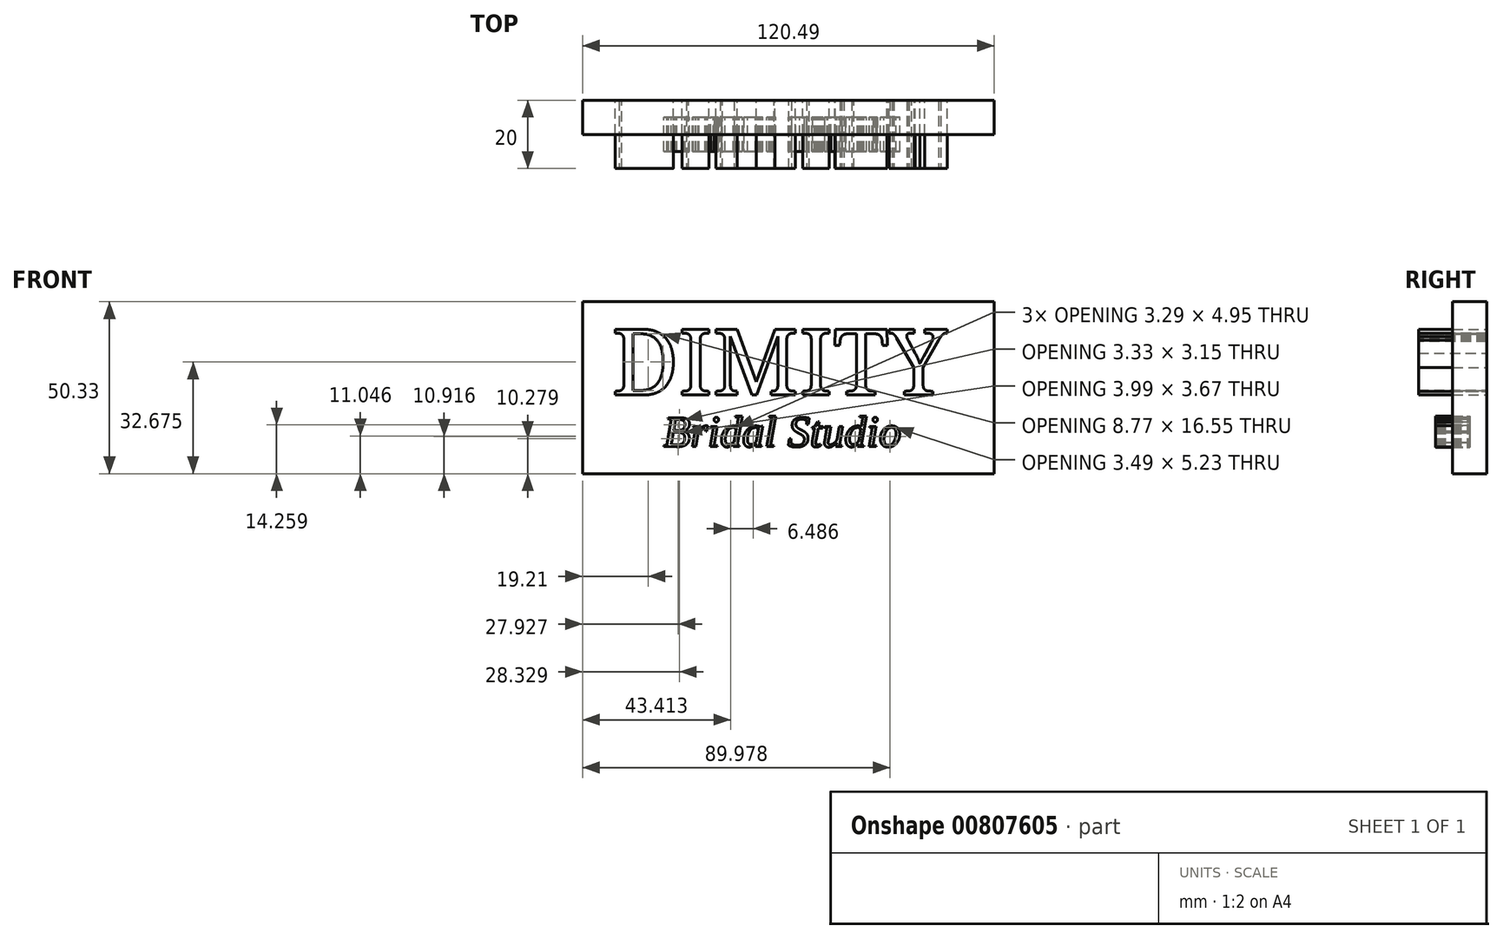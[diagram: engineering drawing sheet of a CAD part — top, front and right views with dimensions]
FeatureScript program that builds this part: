
annotation { "Feature Type Name" : "Feature", "Feature Type Description" : "" }
export const myFeature = defineFeature(function(context is Context, id is Id, definition is map)
    precondition{}
    {
        {
            var Q0;
            Q0=qCreatedBy(makeId("Front.planeOp"),FACE);
            var sketch = newSketch(context, id + "F0", { "sketchPlane" : qUnion([Q0])});
            skText(sketch, "E0", { "text": "DIMITY\n", "fontName": "NotoSerif-Regular.ttf"});
            const initialGuessF0  = {"E0": [-0.05114, -0.00939, 1, 0, 0.01943]};
            skSetInitialGuess(sketch, initialGuessF0);
            skSolve(sketch);
        }
        {
            var Q0;
            Q0=qCreatedBy(makeId("Front.planeOp"),FACE);
            var sketch = newSketch(context, id + "F1", { "sketchPlane" : qUnion([Q0])});
            skText(sketch, "E1", { "text": "Bridal Studio", "fontName": "Tinos-Italic.ttf"});
            const initialGuessF1  = {"E1": [-0.03598, -0.02451, 1, 0, 0.00934]};
            skSetInitialGuess(sketch, initialGuessF1);
            skSolve(sketch);
        }
        {
            var Q0;
            Q0 = qSketchRegion(id + "F0", true);
            extrude(context, id + "F2", {"entities" : qUnion([Q0]), "endBound" : BoundingType.SYMMETRIC, "depth" : 20 * mm, "offsetDistance" : 25 * mm});
        }
        {
            var Q0;
            Q0 = qSketchRegion(id + "F1", true);
            extrude(context, id + "F3", {"entities" : qUnion([Q0]), "endBound" : BoundingType.SYMMETRIC, "depth" : 10 * mm, "offsetDistance" : 25 * mm});
        }
        {
            var Q0;
            Q0=qCreatedBy(makeId("Front.planeOp"),FACE);
            var sketch = newSketch(context, id + "F4", { "sketchPlane" : qUnion([Q0])});
            skLineSegment(sketch, "E2.bottom", {"start": v(-59.65, 17.91) * mm, "end": v(60.84, 17.91) * mm});
            skLineSegment(sketch, "E2.top", {"start": v(-59.65, -32.42) * mm, "end": v(60.84, -32.42) * mm});
            skLineSegment(sketch, "E2.left", {"start": v(-59.65, 17.91) * mm, "end": v(-59.65, -32.42) * mm});
            skLineSegment(sketch, "E2.right", {"start": v(60.84, 17.91) * mm, "end": v(60.84, -32.42) * mm});
            skSolve(sketch);
        }
        {
            var Q0;
            Q0=makeQuery(id+"F4.imprint","IMPRINT",FACE,{"disambiguationData":[TD([[makeQuery(id+"F4.imprint","IMPRINT",EDGE,{"derivedFrom":sQuery(id+"F4.wireOp",EDGE,"E2.bottom")}),-1.0]])]});
            var Q1;
            Q1=makeQuery(id+"F2.opExtrude","CAP_FACE",FACE,{"disambiguationData":[OSD([sQuery(id+"F0.wireOp",EDGE,"E0.sketch_text.stroke-0"),sQuery(id+"F0.wireOp",EDGE,"E0.sketch_text.stroke-1"),sQuery(id+"F0.wireOp",EDGE,"E0.sketch_text.stroke-2"),sQuery(id+"F0.wireOp",EDGE,"E0.sketch_text.stroke-3"),sQuery(id+"F0.wireOp",EDGE,"E0.sketch_text.stroke-4"),sQuery(id+"F0.wireOp",EDGE,"E0.sketch_text.stroke-5"),sQuery(id+"F0.wireOp",EDGE,"E0.sketch_text.stroke-6"),sQuery(id+"F0.wireOp",EDGE,"E0.sketch_text.stroke-7"),sQuery(id+"F0.wireOp",EDGE,"E0.sketch_text.stroke-8"),sQuery(id+"F0.wireOp",EDGE,"E0.sketch_text.stroke-9"),sQuery(id+"F0.wireOp",EDGE,"E0.sketch_text.stroke-10"),sQuery(id+"F0.wireOp",EDGE,"E0.sketch_text.stroke-11"),sQuery(id+"F0.wireOp",EDGE,"E0.sketch_text.stroke-12"),sQuery(id+"F0.wireOp",EDGE,"E0.sketch_text.stroke-13"),sQuery(id+"F0.wireOp",EDGE,"E0.sketch_text.stroke-14"),sQuery(id+"F0.wireOp",EDGE,"E0.sketch_text.stroke-15"),sQuery(id+"F0.wireOp",EDGE,"E0.sketch_text.stroke-16"),sQuery(id+"F0.wireOp",EDGE,"E0.sketch_text.stroke-17"),sQuery(id+"F0.wireOp",EDGE,"E0.sketch_text.stroke-18"),sQuery(id+"F0.wireOp",EDGE,"E0.sketch_text.stroke-19"),sQuery(id+"F0.wireOp",EDGE,"E0.sketch_text.stroke-20"),sQuery(id+"F0.wireOp",EDGE,"E0.sketch_text.stroke-21"),sQuery(id+"F0.wireOp",EDGE,"E0.sketch_text.stroke-22"),sQuery(id+"F0.wireOp",EDGE,"E0.sketch_text.stroke-23"),sQuery(id+"F0.wireOp",EDGE,"E0.sketch_text.stroke-24"),sQuery(id+"F0.wireOp",EDGE,"E0.sketch_text.stroke-25"),sQuery(id+"F0.wireOp",EDGE,"E0.sketch_text.stroke-26"),sQuery(id+"F0.wireOp",EDGE,"E0.sketch_text.stroke-27"),sQuery(id+"F0.wireOp",EDGE,"E0.sketch_text.stroke-28"),sQuery(id+"F0.wireOp",EDGE,"E0.sketch_text.stroke-29"),sQuery(id+"F0.wireOp",EDGE,"E0.sketch_text.stroke-30"),sQuery(id+"F0.wireOp",EDGE,"E0.sketch_text.stroke-31")])],"isStart":true});
            extrude(context, id + "F5", {"entities" : qUnion([Q0]), "endBound" : BoundingType.UP_TO_SURFACE, "oppositeDirection" : true, "depth" : 25 * mm, "endBoundEntityFace" : qUnion([Q1]), "offsetDistance" : 25 * mm});
        }
    });
